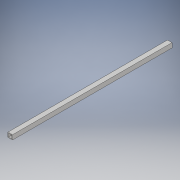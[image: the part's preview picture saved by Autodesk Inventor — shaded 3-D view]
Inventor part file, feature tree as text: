
AUTODESK INVENTOR PART (.ipt)
format: ipt  version: 2018 (Build 220112000, 112)  size: 98,304 bytes
history: native  units: in
note: dims shown in document units (in); Inventor stores cm internally (conversion verified against a paired STEP export)
features: extrude x1, sketch x1
ambient origin geometry x8: Origin, YZ Plane, XZ Plane, XY Plane, X Axis, Y Axis, Z Axis, Center Point
bodies: Solid1 (feature_tree)
feature tree (2):
  extrude  "Extrusion1"  Depth=1.0in
  sketch  "Sketch1"  dims[d0=1.0in d1=1.0in d2=0.125in d3=35.0in d4=0.0in]
